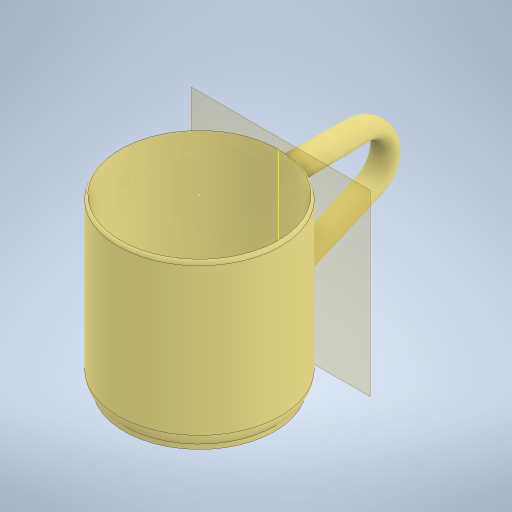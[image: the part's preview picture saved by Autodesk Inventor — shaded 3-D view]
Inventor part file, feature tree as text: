
AUTODESK INVENTOR PART (.ipt)
format: ipt  version: 2024 (Build 280153000, 153)  size: 351,232 bytes
history: native  units: mm
features: sketch x9, other x2, plane x2, revolve x1, shell x1, loft x1, fillet x1, extrude x1
ambient origin geometry x8: Origin, YZ Plane, XZ Plane, XY Plane, X Axis, Y Axis, Z Axis, Center Point
bodies: Solid1 (feature_tree)
feature tree (18):
  other  "CrossSection1"
  other  "CrossSection2"
  revolve  "Revolution1"  [1 undecoded]
  shell  "Shell1"  Thickness=65.0mm
  sketch  "Sketch2"  dims[d3=32.5mm d4=90.0deg d5=1.0mm]
  sketch  "Sketch3"  dims[d6=0.5mm d7=2.0mm d8=0.0mm d9=20.0mm d10=0.5mm d11=2.0mm d12=0.0mm d13=20.0mm]
  sketch  "Sketch4"  dims[d14=12.0mm]
  sketch  "Sketch5"  dims[d17=6.0mm]
  sketch  "Sketch6"  dims[d18=4.0mm]
  plane  "Work Plane1"
  sketch  "Sketch7"  dims[d19=5.0mm]
  plane  "Work Plane2"
  loft  "Loft1"
  fillet  "Fillet1"  Radius=1.0mm
  extrude  "Extrusion1"  Depth=2.0mm TaperAngle=0.0deg
  sketch  "Sketch1"  dims[d0=70.0mm d1=35.0mm d2=65.0mm]
  sketch  "Sketch8"  dims[d20=3.0mm]
  sketch  "Sketch9"  dims[d21=0.0mm d22=90.0deg d23=0.0mm d24=90.0deg d25=0.0mm d26=90.0deg d27=2.0mm d28=65.0mm d29=62.0mm d30=2.0mm d31=0.0mm]
note: 1 required parameter value undecoded (feature->parameter linkage not recoverable at this tier; creation-order binding heuristic only, values carry confidence <= 0.55)
